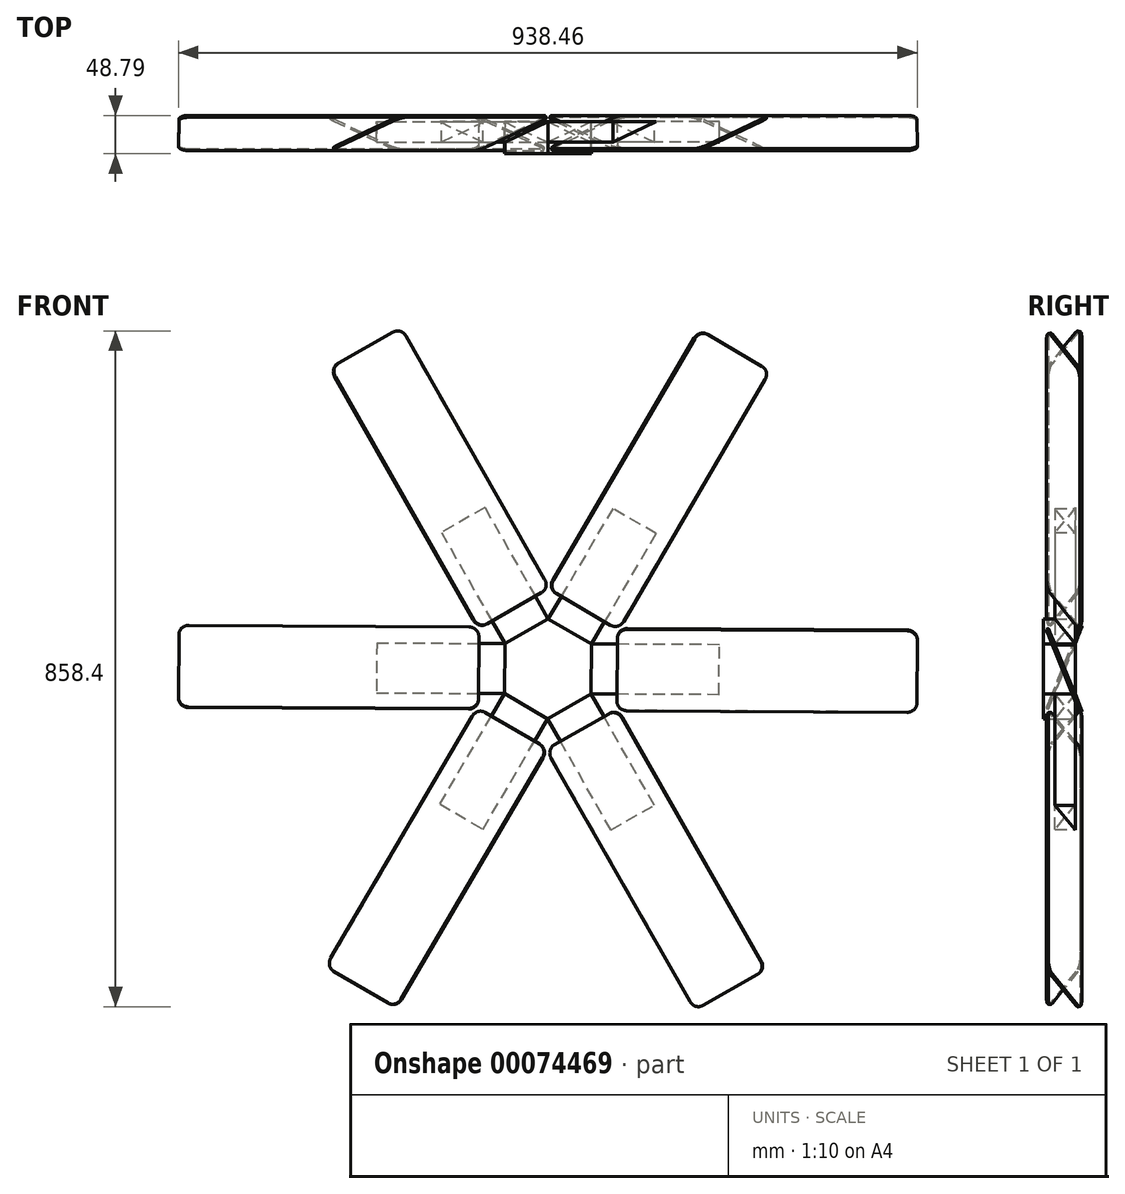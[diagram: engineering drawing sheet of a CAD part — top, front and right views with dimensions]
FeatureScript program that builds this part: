
annotation { "Feature Type Name" : "Feature", "Feature Type Description" : "" }
export const myFeature = defineFeature(function(context is Context, id is Id, definition is map)
    precondition{}
    {
        {
            var Q0;
            Q0=qCreatedBy(makeId("Front.planeOp"),FACE);
            var sketch = newSketch(context, id + "F0", { "sketchPlane" : qUnion([Q0])});
            skCircle(sketch, "E0.cCircle", {"center": v(0, 0) * mm, "radius": 55 * mm, "construction": true});
            skLineSegment(sketch, "E0.0", {"start": v(0.36, 63.5) * mm, "end": v(55.17, 31.44) * mm});
            skLineSegment(sketch, "E0.1", {"start": v(55.17, 31.44) * mm, "end": v(54.81, -32.06) * mm});
            skLineSegment(sketch, "E0.2", {"start": v(54.81, -32.06) * mm, "end": v(-0.36, -63.5) * mm});
            skLineSegment(sketch, "E0.3", {"start": v(-0.36, -63.5) * mm, "end": v(-55.17, -31.44) * mm});
            skLineSegment(sketch, "E0.4", {"start": v(-55.17, -31.44) * mm, "end": v(-54.81, 32.06) * mm});
            skLineSegment(sketch, "E0.5", {"start": v(-54.81, 32.06) * mm, "end": v(0.36, 63.5) * mm});
            skPoint(sketch, "E0.0.midPoint", {"position": v(27.76, 47.47) * mm});
            skSolve(sketch);
        }
        {
            var Q0;
            Q0 = qSketchRegion(id + "F0", true);
            extrude(context, id + "F1", {"entities" : qUnion([Q0]), "depth" : 40.64 * mm});
        }
        {
            var Q0;
            Q0=makeQuery(id+"F1.opExtrude","SWEPT_FACE",FACE,{"disambiguationData":[OSD([sQuery(id+"F0.wireOp",EDGE,"E0.0")])]});
            var sketch = newSketch(context, id + "F2", { "sketchPlane" : qUnion([Q0])});
            skLineSegment(sketch, "E1", {"start": v(31.75, 0) * mm, "end": v(-31.75, -25.9) * mm});
            skLineSegment(sketch, "E2", {"start": v(-31.75, -25.9) * mm, "end": v(-31.75, 0) * mm});
            skLineSegment(sketch, "E3", {"start": v(-31.75, 0) * mm, "end": v(31.75, 0) * mm});
            skSolve(sketch);
        }
        {
            var Q0;
            Q0 = qSketchRegion(id + "F2", true);
            extrude(context, id + "F3", {"entities" : qUnion([Q0]), "depth" : 162.56 * mm});
        }
        {
            var Q0;
            Q0=qCreatedBy(makeId("Right.planeOp"),FACE);
            var sketch = newSketch(context, id + "F4", { "sketchPlane" : qUnion([Q0])});
            skLineSegment(sketch, "E4", {"start": v(0, 0) * mm, "end": v(-110.22, 0) * mm});
            skSolve(sketch);
        }
        {
            var Q0;
            Q0=makeQuery(id+"F3.opExtrude","SWEPT_FACE",FACE,{"disambiguationData":[OSD([sQuery(id+"F2.wireOp",EDGE,"E1")])]});
            var sketch = newSketch(context, id + "F5", { "sketchPlane" : qUnion([Q0])});
            skLineSegment(sketch, "E5", {"start": v(79.37, 53.96) * mm, "end": v(6.36, 100.08) * mm});
            skPoint(sketch, "E5.endSnap0", {"position": v(90.11, 97.63) * mm});
            skLineSegment(sketch, "E6", {"start": v(96.9, 57.92) * mm, "end": v(286.8, 358.56) * mm});
            skLineSegment(sketch, "E7", {"start": v(282.84, 376.08) * mm, "end": v(209.83, 422.2) * mm});
            skLineSegment(sketch, "E8", {"start": v(192.3, 418.25) * mm, "end": v(2.4, 117.6) * mm});
            skLineSegment(sketch, "E9", {"start": v(112.05, 186.54) * mm, "end": v(68.31, 117.3) * mm, "construction": true});
            skPoint(sketch, "E10.visualSharp", {"position": v(293.58, 369.3) * mm});
            skArc(sketch, "E10.filletArc", {"start": v(286.8, 358.56) * mm, "mid": v(288.45, 368.14) * mm, "end": v(282.84, 376.08) * mm});
            skPoint(sketch, "E11.visualSharp", {"position": v(90.11, 47.18) * mm});
            skArc(sketch, "E11.filletArc", {"start": v(79.37, 53.96) * mm, "mid": v(88.95, 52.31) * mm, "end": v(96.9, 57.92) * mm});
            skPoint(sketch, "E12.visualSharp", {"position": v(199.1, 428.99) * mm});
            skArc(sketch, "E12.filletArc", {"start": v(209.83, 422.2) * mm, "mid": v(200.25, 423.85) * mm, "end": v(192.3, 418.25) * mm});
            skPoint(sketch, "E13.visualSharp", {"position": v(-4.38, 106.87) * mm});
            skArc(sketch, "E13.filletArc", {"start": v(2.4, 117.6) * mm, "mid": v(0.75, 108.02) * mm, "end": v(6.36, 100.08) * mm});
            skSolve(sketch);
        }
        {
            var Q0;
            Q0 = qSketchRegion(id + "F5", true);
            extrude(context, id + "F6", {"entities" : qUnion([Q0]), "depth" : 2.54 * mm});
        }
        {
            var Q0;
            Q0=makeQuery(id+"F3.opExtrude","SWEPT_BODY",BODY,{"disambiguationData":[OSD([sQuery(id+"F2.wireOp",EDGE,"E1"),sQuery(id+"F2.wireOp",EDGE,"E2"),sQuery(id+"F2.wireOp",EDGE,"E3")])]});
            var Q1;
            Q1=makeQuery(id+"F6.opExtrude","SWEPT_BODY",BODY,{"disambiguationData":[OSD([sQuery(id+"F5.wireOp",EDGE,"E5"),sQuery(id+"F5.wireOp",EDGE,"E6"),sQuery(id+"F5.wireOp",EDGE,"E7"),sQuery(id+"F5.wireOp",EDGE,"E8"),sQuery(id+"F5.wireOp",EDGE,"E10.filletArc"),sQuery(id+"F5.wireOp",EDGE,"E11.filletArc"),sQuery(id+"F5.wireOp",EDGE,"E12.filletArc"),sQuery(id+"F5.wireOp",EDGE,"E13.filletArc")])]});
            var Q2;
            Q2=sQuery(id+"F4.wireOp",EDGE,"E4");
            circularPattern(context, id + "F7", {"entities" : qUnion([Q0, Q1]), "axis" : qUnion([Q2]), "angle" : 60 * degree, "instanceCount" : 6});
        }
    });
